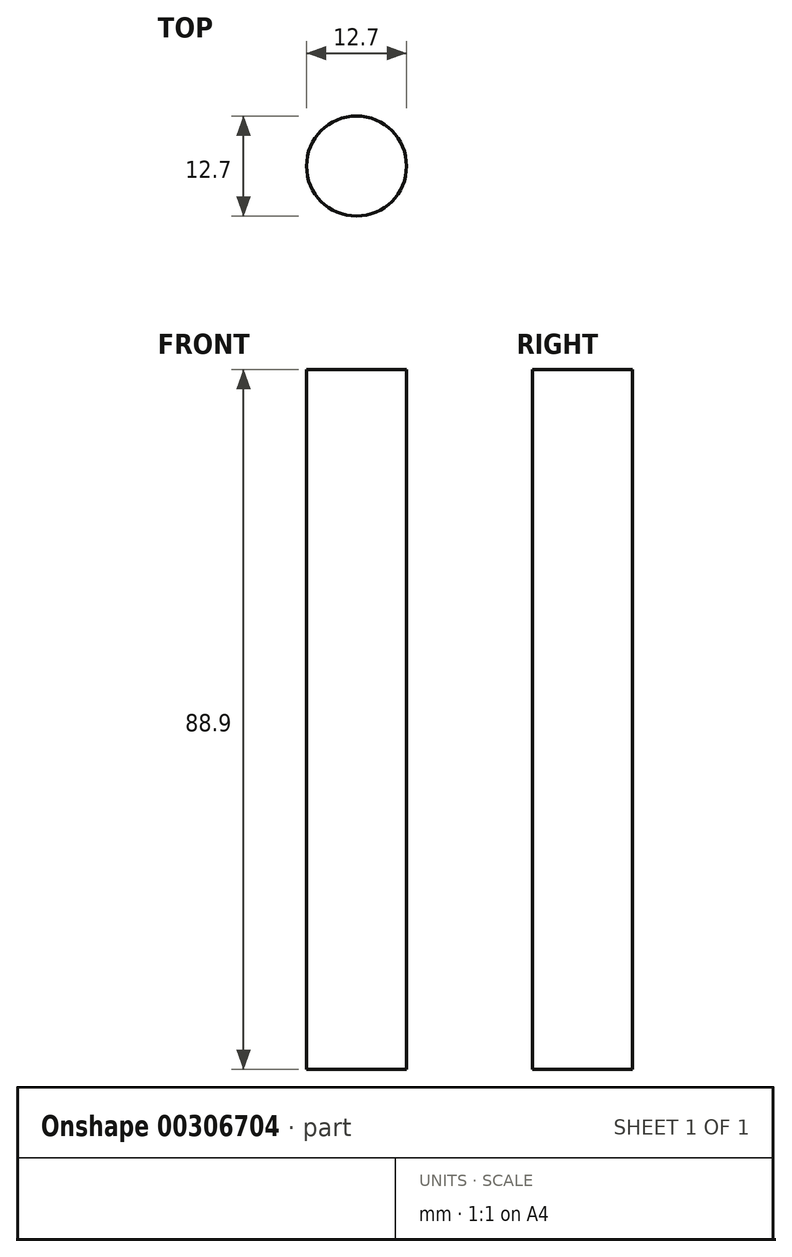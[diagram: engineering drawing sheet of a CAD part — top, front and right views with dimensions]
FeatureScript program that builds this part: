
annotation { "Feature Type Name" : "Feature", "Feature Type Description" : "" }
export const myFeature = defineFeature(function(context is Context, id is Id, definition is map)
    precondition{}
    {
        {
            var Q0;
            Q0=qCreatedBy(makeId("Top.planeOp"),FACE);
            var sketch = newSketch(context, id + "F0", { "sketchPlane" : qUnion([Q0])});
            skCircle(sketch, "E0", {"center": v(0, 0) * mm, "radius": 6.35 * mm});
            skSolve(sketch);
        }
        {
            var Q0;
            Q0=makeQuery(id+"F0.imprint","IMPRINT",FACE,{"disambiguationData":[TD([[makeQuery(id+"F0.imprint","IMPRINT",EDGE,{"derivedFrom":sQuery(id+"F0.wireOp",EDGE,"E0")}),1.0]])]});
            extrude(context, id + "F1", {"entities" : qUnion([Q0]), "depth" : 88.9 * mm});
        }
    });
